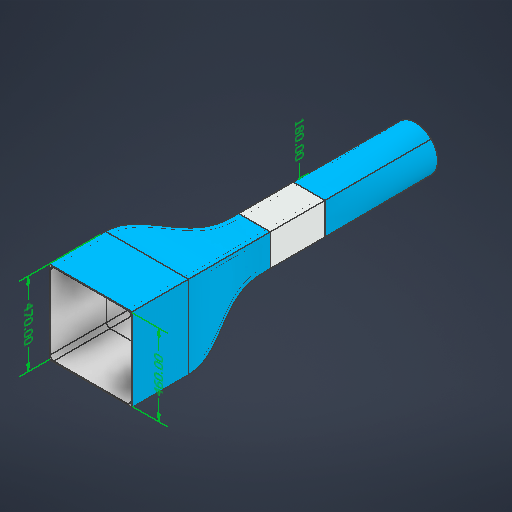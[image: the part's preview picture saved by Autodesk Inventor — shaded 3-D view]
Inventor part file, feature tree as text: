
AUTODESK INVENTOR PART (.ipt)
format: ipt  version: 2025 (Build 290162010, 162A)  size: 521,216 bytes
history: native  units: mm
features: other x8, sketch x8, plane x4, loft x4, extrude x3, fillet x1
ambient origin geometry x8: Origin, YZ Plane, XZ Plane, XY Plane, X Axis, Y Axis, Z Axis, Center Point
bodies: Solid1 (feature_tree)
feature tree (28):
  other  "Annotations"
  extrude  "Extrusion1"  Depth=180.0mm
  plane  "Work Plane1"
  sketch  "Sketch2"  dims[d2=5.0mm d3=310.0mm d4=0.0mm]
  plane  "Work Plane2"
  sketch  "Sketch3"  dims[d11=605.0mm d12=250.0mm]
  sketch  "Sketch4"  dims[d14=-90.0mm d15=605.0mm]
  loft  "Loft1"
  loft  "Loft2"
  plane  "Work Plane4"
  sketch  "Sketch5"  dims[d16=0.0mm d17=90.0deg d18=0.0mm d19=90.0deg]
  sketch  "Sketch6"  dims[d20=5.0mm d21=0.0mm d22=90.0deg d23=0.0mm d24=90.0deg]
  sketch  "Sketch7"  dims[d27=470.0mm d28=470.0mm]
  loft  "Loft3"
  loft  "Loft4"
  extrude  "Extrusion2"  TaperAngle=0.0deg  [1 undecoded]
  fillet  "Fillet1"  [1 undecoded]
  plane  "Work Plane5"
  extrude  "Extrusion3"  Depth=470.0mm
  sketch  "Sketch1"  dims[d0=180.0mm d1=180.0mm]
  other  "Edges1"
  other  "Edges2"
  sketch  "Sketch8"  dims[d29=5.0mm d31=90.0deg d38=320.0mm d39=0.0mm d40=20.0mm d43=320.0mm d44=0.0mm d45=10.0mm d46=10.0mm d47=90.0deg d48=10.0mm d49=90.0deg d50=10.0mm d51=90.0deg d56=470.0mm d65=4.815112mm d66=3.504431mm d67=460.0mm d68=2.29905mm d69=6.653648mm d70=180.0mm d41=0.0mm d42=0.0mm]
  other  "Edges3"
  other  "Edges4"
  other  "Linear Dimension 2"
  other  "Linear Dimension 3"
  other  "Linear Dimension 4"
note: 2 required parameter values undecoded (feature->parameter linkage not recoverable at this tier; creation-order binding heuristic only, values carry confidence <= 0.55)
